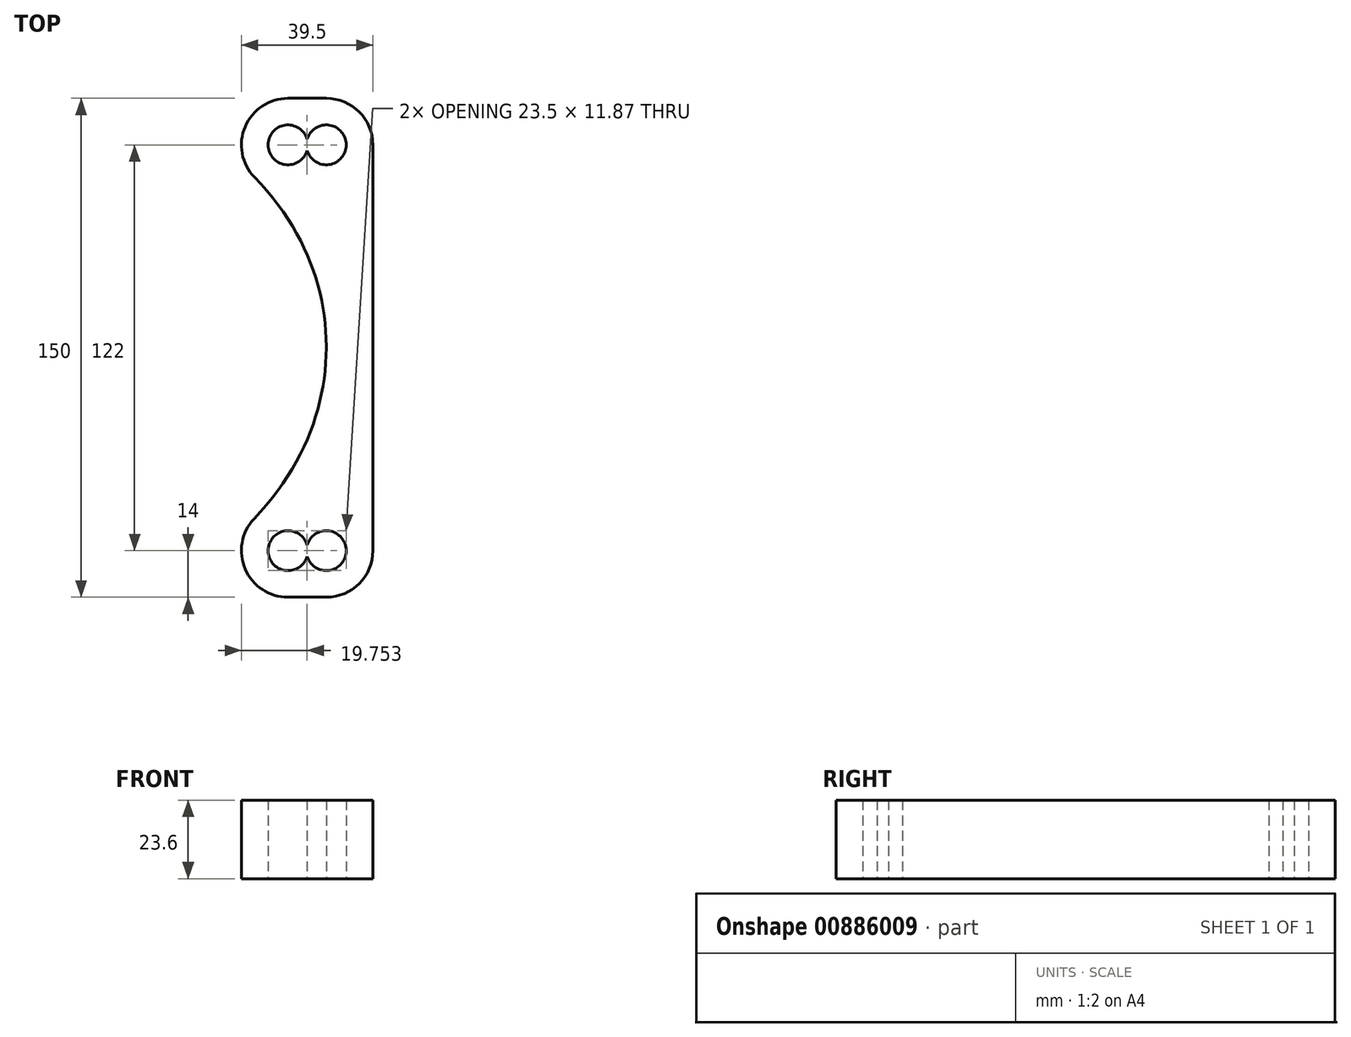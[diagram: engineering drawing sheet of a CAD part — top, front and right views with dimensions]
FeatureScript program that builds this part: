
annotation { "Feature Type Name" : "Feature", "Feature Type Description" : "" }
export const myFeature = defineFeature(function(context is Context, id is Id, definition is map)
    precondition{}
    {
        {
            var Q0;
            Q0=qCreatedBy(makeId("Top.planeOp"),FACE);
            var sketch = newSketch(context, id + "F0", { "sketchPlane" : qUnion([Q0])});
            skCircle(sketch, "E0", {"center": v(0, 0) * mm, "radius": 169 * mm, "construction": true});
            skCircle(sketch, "E1", {"center": v(0, 0) * mm, "radius": 70 * mm, "construction": true});
            skCircle(sketch, "E2", {"center": v(-34.34, 61) * mm, "radius": 6 * mm});
            skCircle(sketch, "E3", {"center": v(-34.34, -61) * mm, "radius": 6 * mm});
            skLineSegment(sketch, "E4", {"start": v(-34.34, -61) * mm, "end": v(-34.34, 61) * mm});
            skLineSegment(sketch, "E5", {"start": v(-169, 0) * mm, "end": v(-122, 0) * mm});
            skLineSegment(sketch, "E6", {"start": v(-70, 0) * mm, "end": v(-122, 0) * mm});
            skCircle(sketch, "E7", {"center": v(-45.84, 61) * mm, "radius": 6 * mm});
            skCircle(sketch, "E8", {"center": v(-45.84, -61) * mm, "radius": 6 * mm});
            skLineSegment(sketch, "E9", {"start": v(-34.34, -61) * mm, "end": v(-45.84, -61) * mm});
            skLineSegment(sketch, "E10", {"start": v(-34.34, 61) * mm, "end": v(-45.84, 61) * mm});
            skLineSegment(sketch, "E11", {"start": v(-45.84, -61) * mm, "end": v(-45.84, 61) * mm, "construction": true});
            skCircle(sketch, "E12", {"center": v(-34.34, 61) * mm, "radius": 14 * mm});
            skCircle(sketch, "E13", {"center": v(-34.34, -61) * mm, "radius": 14 * mm});
            skCircle(sketch, "E14", {"center": v(-45.84, -61) * mm, "radius": 14 * mm});
            skCircle(sketch, "E15", {"center": v(-45.84, 61) * mm, "radius": 14 * mm});
            skLineSegment(sketch, "E16", {"start": v(-45.84, 75) * mm, "end": v(-34.34, 75) * mm});
            skLineSegment(sketch, "E17", {"start": v(-45.84, -75) * mm, "end": v(-34.34, -75) * mm});
            skLineSegment(sketch, "E18", {"start": v(-20.34, 61) * mm, "end": v(-20.34, -61) * mm});
            skFitSpline(sketch, "E19", {"points": [v(-62.93, 57.83) * mm, v(-34.34, 0) * mm, v(-62.9, -58.05) * mm], "startDerivative": vector(120.8, -102.14) * mm, "endDerivative": vector(-118.8, -105.22) * mm});
            skSolve(sketch);
        }
        {
            var Q0;
            Q0=qSketchRegion(id+"F0",true);
            var Q1;
            {var subQ0=sQuery(id+"F0.wireOp",EDGE,"E15");var subQ1=sQuery(id+"F0.wireOp",EDGE,"E2");var subQ2=makeQuery(id+"F0.imprint","INTERSECT",VERTEX,{"disambiguationData":[OD(1.0)],"derivedFrom":[subQ1,subQ0]});Q1=makeQuery(id+"F0.imprint","IMPRINT",FACE,{"disambiguationData":[TD([[makeQuery(id+"F0.imprint","IMPRINT",EDGE,{"disambiguationData":[TD([[subQ2,-1.0]])],"derivedFrom":subQ1}),-1.0]])]});}
            var Q2;
            {var subQ0=sQuery(id+"F0.wireOp",EDGE,"E14");var subQ1=sQuery(id+"F0.wireOp",EDGE,"E3");var subQ2=makeQuery(id+"F0.imprint","INTERSECT",VERTEX,{"disambiguationData":[OD(0.0)],"derivedFrom":[subQ1,subQ0]});Q2=makeQuery(id+"F0.imprint","IMPRINT",FACE,{"disambiguationData":[TD([[makeQuery(id+"F0.imprint","IMPRINT",EDGE,{"disambiguationData":[TD([[subQ2,1.0]])],"derivedFrom":subQ1}),-1.0]])]});}
            var Q3;
            {var subQ3=sQuery(id+"F0.wireOp",EDGE,"E14");var subQ6=sQuery(id+"F0.wireOp",EDGE,"E3");var subQ9=makeQuery(id+"F0.imprint","INTERSECT",VERTEX,{"disambiguationData":[OD(0.0)],"derivedFrom":[subQ6,subQ3]});Q3=makeQuery(id+"F0.imprint","IMPRINT",FACE,{"disambiguationData":[TD([[makeQuery(id+"F0.imprint","IMPRINT",EDGE,{"disambiguationData":[TD([[subQ9,-1.0]])],"derivedFrom":subQ6}),-1.0]])]});}
            var Q4;
            {var subQ0=sQuery(id+"F0.wireOp",EDGE,"E7");var subQ1=sQuery(id+"F0.wireOp",EDGE,"E2");var subQ2=makeQuery(id+"F0.imprint","INTERSECT",VERTEX,{"disambiguationData":[OD(0.0)],"derivedFrom":[subQ1,subQ0]});Q4=makeQuery(id+"F0.imprint","IMPRINT",FACE,{"disambiguationData":[TD([[makeQuery(id+"F0.imprint","IMPRINT",EDGE,{"disambiguationData":[TD([[subQ2,1.0]])],"derivedFrom":subQ1}),-1.0]])]});}
            var Q5;
            {var subQ1=sQuery(id+"F0.wireOp",EDGE,"E7");var subQ5=sQuery(id+"F0.wireOp",EDGE,"E2");var subQ6=makeQuery(id+"F0.imprint","INTERSECT",VERTEX,{"disambiguationData":[OD(1.0)],"derivedFrom":[subQ5,subQ1]});Q5=makeQuery(id+"F0.imprint","IMPRINT",FACE,{"disambiguationData":[TD([[makeQuery(id+"F0.imprint","IMPRINT",EDGE,{"disambiguationData":[TD([[subQ6,-1.0]])],"derivedFrom":subQ5}),-1.0]])]});}
            var Q6;
            {var subQ0=sQuery(id+"F0.wireOp",EDGE,"E12");var subQ1=sQuery(id+"F0.wireOp",EDGE,"E4");var subQ2=makeQuery(id+"F0.imprint","INTERSECT",VERTEX,{"derivedFrom":[subQ1,subQ0]});Q6=makeQuery(id+"F0.imprint","IMPRINT",FACE,{"disambiguationData":[TD([[makeQuery(id+"F0.imprint","IMPRINT",EDGE,{"disambiguationData":[TD([[subQ2,-1.0]])],"derivedFrom":subQ1}),1.0]])]});}
            var Q7;
            {var subQ0=sQuery(id+"F0.wireOp",EDGE,"E8");var subQ1=sQuery(id+"F0.wireOp",EDGE,"E3");var subQ2=makeQuery(id+"F0.imprint","INTERSECT",VERTEX,{"disambiguationData":[OD(1.0)],"derivedFrom":[subQ1,subQ0]});Q7=makeQuery(id+"F0.imprint","IMPRINT",FACE,{"disambiguationData":[TD([[makeQuery(id+"F0.imprint","IMPRINT",EDGE,{"disambiguationData":[TD([[subQ2,-1.0]])],"derivedFrom":subQ1}),-1.0]])]});}
            var Q8;
            {var subQ0=sQuery(id+"F0.wireOp",EDGE,"E14");var subQ1=sQuery(id+"F0.wireOp",EDGE,"E4");var subQ2=makeQuery(id+"F0.imprint","INTERSECT",VERTEX,{"derivedFrom":[subQ1,subQ0]});Q8=makeQuery(id+"F0.imprint","IMPRINT",FACE,{"disambiguationData":[TD([[makeQuery(id+"F0.imprint","IMPRINT",EDGE,{"disambiguationData":[TD([[subQ2,-1.0]])],"derivedFrom":subQ1}),1.0]])]});}
            var Q9;
            {var subQ1=sQuery(id+"F0.wireOp",EDGE,"E3");var subQ7=sQuery(id+"F0.wireOp",EDGE,"E4");var subQ8=makeQuery(id+"F0.imprint","INTERSECT",VERTEX,{"derivedFrom":[subQ1,subQ7]});Q9=makeQuery(id+"F0.imprint","IMPRINT",FACE,{"disambiguationData":[TD([[makeQuery(id+"F0.imprint","IMPRINT",EDGE,{"disambiguationData":[TD([[subQ8,-1.0]])],"derivedFrom":subQ1}),-1.0]])]});}
            var Q10;
            {var subQ0=sQuery(id+"F0.wireOp",EDGE,"E4");var subQ1=sQuery(id+"F0.wireOp",EDGE,"E2");var subQ2=makeQuery(id+"F0.imprint","INTERSECT",VERTEX,{"derivedFrom":[subQ1,subQ0]});Q10=makeQuery(id+"F0.imprint","IMPRINT",FACE,{"disambiguationData":[TD([[makeQuery(id+"F0.imprint","IMPRINT",EDGE,{"disambiguationData":[TD([[subQ2,-1.0]])],"derivedFrom":subQ1}),-1.0]])]});}
            extrude(context, id + "F1", {"entities" : qUnion([Q0, Q1, Q2, Q3, Q4, Q5, Q6, Q7, Q8, Q9, Q10]), "depth" : 23.6 * mm, "offsetDistance" : 25 * mm});
        }
    });
